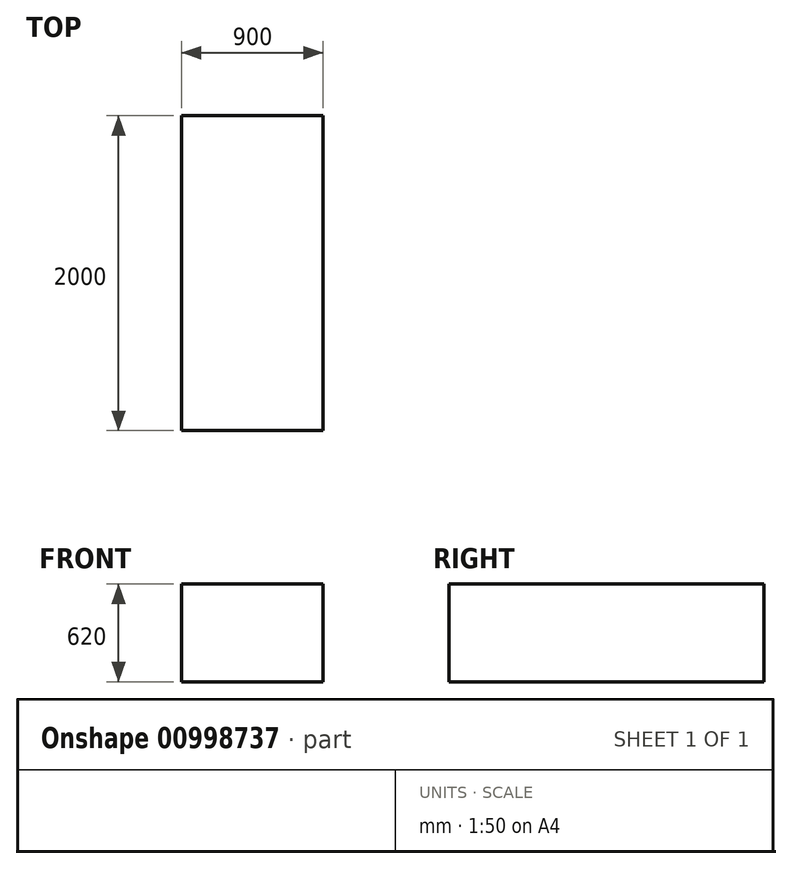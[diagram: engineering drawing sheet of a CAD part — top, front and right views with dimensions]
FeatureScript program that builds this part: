
annotation { "Feature Type Name" : "Feature", "Feature Type Description" : "" }
export const myFeature = defineFeature(function(context is Context, id is Id, definition is map)
    precondition{}
    {
        {
            var Q0;
            Q0=qCreatedBy(makeId("Top.planeOp"),FACE);
            var sketch = newSketch(context, id + "F0", { "sketchPlane" : qUnion([Q0])});
            skLineSegment(sketch, "E0.bottom", {"start": v(0, 0) * mm, "end": v(900, 0) * mm});
            skLineSegment(sketch, "E0.top", {"start": v(0, 2000) * mm, "end": v(900, 2000) * mm});
            skLineSegment(sketch, "E0.left", {"start": v(0, 0) * mm, "end": v(0, 2000) * mm});
            skLineSegment(sketch, "E0.right", {"start": v(900, 0) * mm, "end": v(900, 2000) * mm});
            skSolve(sketch);
        }
        {
            var Q0;
            Q0=makeQuery(id+"F0.imprint","IMPRINT",FACE,{"disambiguationData":[TD([[makeQuery(id+"F0.imprint","IMPRINT",EDGE,{"derivedFrom":sQuery(id+"F0.wireOp",EDGE,"E0.bottom")}),1.0]])]});
            extrude(context, id + "F1", {"entities" : qUnion([Q0]), "depth" : 620 * mm, "offsetDistance" : 25 * mm});
        }
    });
